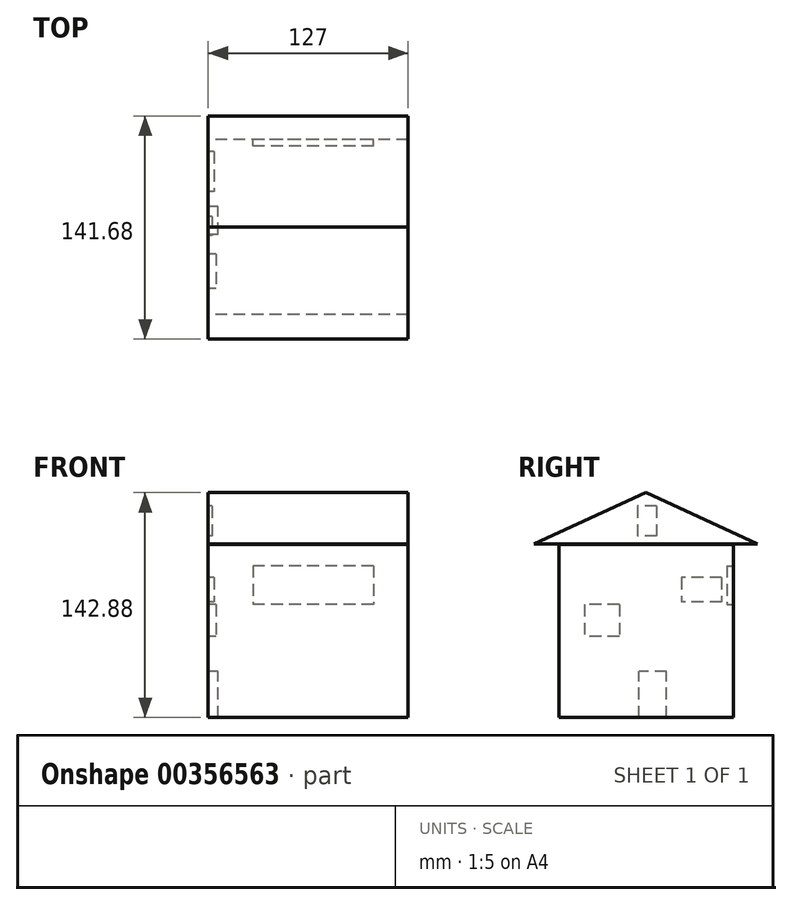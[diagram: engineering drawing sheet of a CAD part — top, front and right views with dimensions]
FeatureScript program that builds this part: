
annotation { "Feature Type Name" : "Feature", "Feature Type Description" : "" }
export const myFeature = defineFeature(function(context is Context, id is Id, definition is map)
    precondition{}
    {
        {
            var Q0;
            Q0=qCreatedBy(makeId("Right.planeOp"),FACE);
            var sketch = newSketch(context, id + "F0", { "sketchPlane" : qUnion([Q0])});
            skLineSegment(sketch, "E0.bottom", {"start": v(-55.44, 49.94) * mm, "end": v(55.44, 49.94) * mm});
            skLineSegment(sketch, "E0.top", {"start": v(-55.44, -59.87) * mm, "end": v(55.44, -59.87) * mm});
            skLineSegment(sketch, "E0.left", {"start": v(-55.44, 49.94) * mm, "end": v(-55.44, -59.87) * mm});
            skLineSegment(sketch, "E0.right", {"start": v(55.44, 49.94) * mm, "end": v(55.44, -59.87) * mm});
            skSolve(sketch);
        }
        {
            var Q0;
            Q0=makeQuery(id+"F0.imprint","IMPRINT",FACE,{"disambiguationData":[TD([[makeQuery(id+"F0.imprint","IMPRINT",EDGE,{"derivedFrom":sQuery(id+"F0.wireOp",EDGE,"E0.bottom")}),-1.0]])]});
            extrude(context, id + "F1", {"entities" : qUnion([Q0]), "depth" : 127 * mm});
        }
        {
            var Q0;
            Q0=makeQuery(id+"F1.opExtrude","CAP_FACE",FACE,{"disambiguationData":[OSD([sQuery(id+"F0.wireOp",EDGE,"E0.bottom"),sQuery(id+"F0.wireOp",EDGE,"E0.top"),sQuery(id+"F0.wireOp",EDGE,"E0.left"),sQuery(id+"F0.wireOp",EDGE,"E0.right")])],"isStart":true});
            var sketch = newSketch(context, id + "F2", { "sketchPlane" : qUnion([Q0])});
            skLineSegment(sketch, "E1.bottom", {"start": v(-13, -59.87) * mm, "end": v(4.68, -59.87) * mm});
            skLineSegment(sketch, "E1.top", {"start": v(-13, -30.5) * mm, "end": v(4.68, -30.5) * mm});
            skLineSegment(sketch, "E1.left", {"start": v(-13, -59.87) * mm, "end": v(-13, -30.5) * mm});
            skLineSegment(sketch, "E1.right", {"start": v(4.68, -59.87) * mm, "end": v(4.68, -30.5) * mm});
            skSolve(sketch);
        }
        {
            var Q0;
            Q0=makeQuery(id+"F2.imprint","IMPRINT",FACE,{"disambiguationData":[TD([[makeQuery(id+"F2.imprint","IMPRINT",EDGE,{"derivedFrom":sQuery(id+"F2.wireOp",EDGE,"E1.bottom")}),-1.0]])]});
            extrude(context, id + "F3", {"entities" : qUnion([Q0]), "operationType" : NewBodyOperationType.REMOVE, "oppositeDirection" : true, "depth" : 6.35 * mm});
        }
        {
            var Q0;
            Q0=makeQuery(id+"F1.opExtrude","CAP_FACE",FACE,{"disambiguationData":[OSD([sQuery(id+"F0.wireOp",EDGE,"E0.bottom"),sQuery(id+"F0.wireOp",EDGE,"E0.top"),sQuery(id+"F0.wireOp",EDGE,"E0.left"),sQuery(id+"F0.wireOp",EDGE,"E0.right")])],"isStart":true});
            var sketch = newSketch(context, id + "F4", { "sketchPlane" : qUnion([Q0])});
            skLineSegment(sketch, "E2.bottom", {"start": v(-47.93, 29) * mm, "end": v(-22.42, 29) * mm});
            skLineSegment(sketch, "E2.top", {"start": v(-47.93, 13.7) * mm, "end": v(-22.42, 13.7) * mm});
            skLineSegment(sketch, "E2.left", {"start": v(-47.93, 29) * mm, "end": v(-47.93, 13.7) * mm});
            skLineSegment(sketch, "E2.right", {"start": v(-22.42, 29) * mm, "end": v(-22.42, 13.7) * mm});
            skSolve(sketch);
        }
        {
            var Q0;
            Q0=makeQuery(id+"F4.imprint","IMPRINT",FACE,{"disambiguationData":[TD([[makeQuery(id+"F4.imprint","IMPRINT",EDGE,{"derivedFrom":sQuery(id+"F4.wireOp",EDGE,"E2.bottom")}),-1.0]])]});
            extrude(context, id + "F5", {"entities" : qUnion([Q0]), "operationType" : NewBodyOperationType.REMOVE, "oppositeDirection" : true, "depth" : 3.8 * mm});
        }
        {
            var Q0;
            Q0=makeQuery(id+"F1.opExtrude","CAP_FACE",FACE,{"disambiguationData":[OSD([sQuery(id+"F0.wireOp",EDGE,"E0.bottom"),sQuery(id+"F0.wireOp",EDGE,"E0.top"),sQuery(id+"F0.wireOp",EDGE,"E0.left"),sQuery(id+"F0.wireOp",EDGE,"E0.right")])],"isStart":true});
            var sketch = newSketch(context, id + "F6", { "sketchPlane" : qUnion([Q0])});
            skLineSegment(sketch, "E3.bottom", {"start": v(17.05, 11.81) * mm, "end": v(39.07, 11.81) * mm});
            skLineSegment(sketch, "E3.top", {"start": v(17.05, -8.32) * mm, "end": v(39.07, -8.32) * mm});
            skLineSegment(sketch, "E3.left", {"start": v(17.05, 11.81) * mm, "end": v(17.05, -8.32) * mm});
            skLineSegment(sketch, "E3.right", {"start": v(39.07, 11.81) * mm, "end": v(39.07, -8.32) * mm});
            skSolve(sketch);
        }
        {
            var Q0;
            Q0=makeQuery(id+"F6.imprint","IMPRINT",FACE,{"disambiguationData":[TD([[makeQuery(id+"F6.imprint","IMPRINT",EDGE,{"derivedFrom":sQuery(id+"F6.wireOp",EDGE,"E3.bottom")}),-1.0]])]});
            extrude(context, id + "F7", {"entities" : qUnion([Q0]), "operationType" : NewBodyOperationType.REMOVE, "oppositeDirection" : true, "depth" : 4.83 * mm});
        }
        {
            var Q0;
            Q0=qCreatedBy(makeId("Right.planeOp"),FACE);
            var sketch = newSketch(context, id + "F8", { "sketchPlane" : qUnion([Q0])});
            skLineSegment(sketch, "E4", {"start": v(70.53, 50.3) * mm, "end": v(0, 83.01) * mm});
            skLineSegment(sketch, "E5", {"start": v(0, 83.01) * mm, "end": v(-71.15, 50.3) * mm});
            skLineSegment(sketch, "E6", {"start": v(-71.15, 50.3) * mm, "end": v(70.53, 50.3) * mm});
            skSolve(sketch);
        }
        {
            var Q0;
            Q0=makeQuery(id+"F8.imprint","IMPRINT",FACE,{"disambiguationData":[TD([[makeQuery(id+"F8.imprint","IMPRINT",EDGE,{"derivedFrom":sQuery(id+"F8.wireOp",EDGE,"E4")}),1.0]])]});
            extrude(context, id + "F9", {"entities" : qUnion([Q0]), "depth" : 127 * mm});
        }
        {
            var Q0;
            Q0=makeQuery(id+"F1.opExtrude","SWEPT_FACE",FACE,{"disambiguationData":[OSD([sQuery(id+"F0.wireOp",EDGE,"E0.right")])]});
            var sketch = newSketch(context, id + "F10", { "sketchPlane" : qUnion([Q0])});
            skLineSegment(sketch, "E7.bottom", {"start": v(-104.92, 36.5) * mm, "end": v(-28.63, 36.5) * mm});
            skLineSegment(sketch, "E7.top", {"start": v(-104.92, 12.1) * mm, "end": v(-28.63, 12.1) * mm});
            skLineSegment(sketch, "E7.left", {"start": v(-104.92, 36.5) * mm, "end": v(-104.92, 12.1) * mm});
            skLineSegment(sketch, "E7.right", {"start": v(-28.63, 36.5) * mm, "end": v(-28.63, 12.1) * mm});
            skSolve(sketch);
        }
        {
            var Q0;
            Q0=makeQuery(id+"F10.imprint","IMPRINT",FACE,{"disambiguationData":[TD([[makeQuery(id+"F10.imprint","IMPRINT",EDGE,{"derivedFrom":sQuery(id+"F10.wireOp",EDGE,"E7.bottom")}),-1.0]])]});
            extrude(context, id + "F11", {"entities" : qUnion([Q0]), "operationType" : NewBodyOperationType.REMOVE, "oppositeDirection" : true, "depth" : 4.06 * mm});
        }
        {
            var Q0;
            Q0=makeQuery(id+"F9.opExtrude","CAP_FACE",FACE,{"disambiguationData":[OSD([sQuery(id+"F8.wireOp",EDGE,"E4"),sQuery(id+"F8.wireOp",EDGE,"E5"),sQuery(id+"F8.wireOp",EDGE,"E6")])],"isStart":true});
            var sketch = newSketch(context, id + "F12", { "sketchPlane" : qUnion([Q0])});
            skLineSegment(sketch, "E8.bottom", {"start": v(-6.6, 74.37) * mm, "end": v(5.47, 74.37) * mm});
            skLineSegment(sketch, "E8.top", {"start": v(-6.6, 55.58) * mm, "end": v(5.47, 55.58) * mm});
            skLineSegment(sketch, "E8.left", {"start": v(-6.6, 74.37) * mm, "end": v(-6.6, 55.58) * mm});
            skLineSegment(sketch, "E8.right", {"start": v(5.47, 74.37) * mm, "end": v(5.47, 55.58) * mm});
            skSolve(sketch);
        }
        {
            var Q0;
            Q0=makeQuery(id+"F12.imprint","IMPRINT",FACE,{"disambiguationData":[TD([[makeQuery(id+"F12.imprint","IMPRINT",EDGE,{"derivedFrom":sQuery(id+"F12.wireOp",EDGE,"E8.bottom")}),-1.0]])]});
            extrude(context, id + "F13", {"entities" : qUnion([Q0]), "operationType" : NewBodyOperationType.REMOVE, "oppositeDirection" : true, "depth" : 2.54 * mm});
        }
    });
